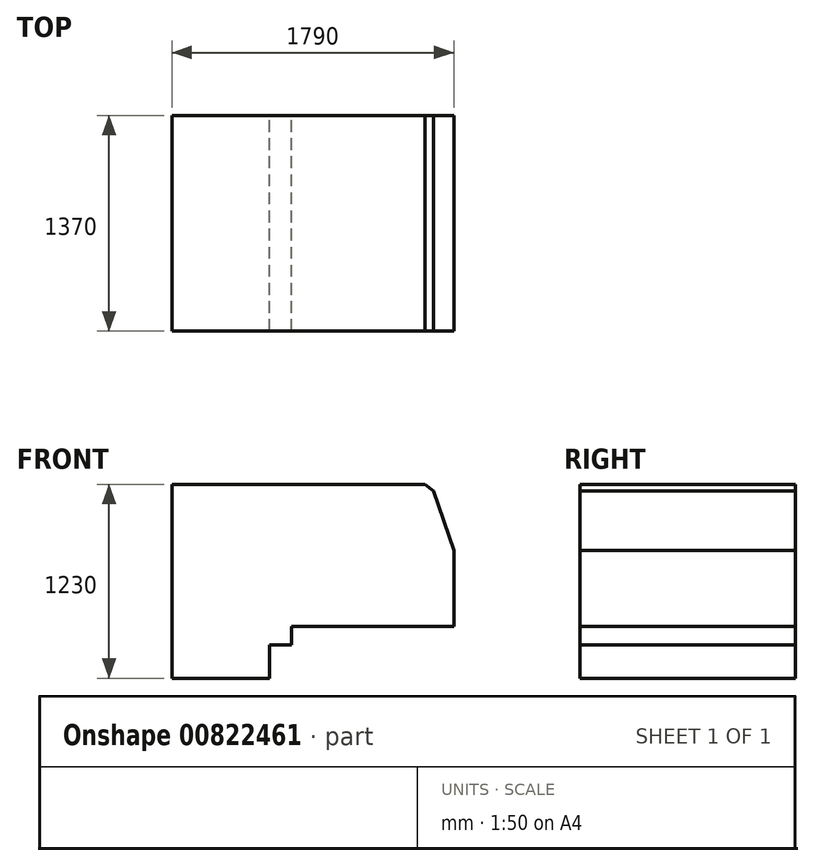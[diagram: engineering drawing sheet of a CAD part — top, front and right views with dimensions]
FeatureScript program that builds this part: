
annotation { "Feature Type Name" : "Feature", "Feature Type Description" : "" }
export const myFeature = defineFeature(function(context is Context, id is Id, definition is map)
    precondition{}
    {
        {
            var Q0;
            Q0=qCreatedBy(makeId("Front.planeOp"),FACE);
            var sketch = newSketch(context, id + "F0", { "sketchPlane" : qUnion([Q0])});
            skLineSegment(sketch, "E0", {"start": v(-929.22, -816.1) * mm, "end": v(-309.4, -816.1) * mm});
            skLineSegment(sketch, "E1", {"start": v(-309.4, -816.1) * mm, "end": v(-309.4, -606.1) * mm});
            skLineSegment(sketch, "E2", {"start": v(-309.4, -606.1) * mm, "end": v(-169.22, -606.1) * mm});
            skLineSegment(sketch, "E3", {"start": v(-169.22, -606.1) * mm, "end": v(-169.22, -486.1) * mm});
            skLineSegment(sketch, "E4", {"start": v(-169.22, -486.1) * mm, "end": v(860.78, -486.1) * mm});
            skLineSegment(sketch, "E5", {"start": v(860.78, -486.1) * mm, "end": v(860.78, -6.1) * mm});
            skLineSegment(sketch, "E6", {"start": v(860.78, -6.1) * mm, "end": v(731.39, 373.9) * mm});
            skLineSegment(sketch, "E7", {"start": v(731.39, 373.9) * mm, "end": v(675.93, 413.9) * mm});
            skLineSegment(sketch, "E8", {"start": v(675.93, 413.9) * mm, "end": v(-929.22, 413.9) * mm});
            skLineSegment(sketch, "E9", {"start": v(-929.22, 413.9) * mm, "end": v(-929.22, -816.1) * mm});
            skSolve(sketch);
        }
        {
            var Q0;
            Q0=makeQuery(id+"F0.imprint","IMPRINT",FACE,{"disambiguationData":[TD([[makeQuery(id+"F0.imprint","IMPRINT",EDGE,{"derivedFrom":sQuery(id+"F0.wireOp",EDGE,"E0")}),1.0]])]});
            extrude(context, id + "F1", {"entities" : qUnion([Q0]), "endBound" : BoundingType.SYMMETRIC, "depth" : 1370 * mm, "offsetDistance" : 25 * mm});
        }
    });
